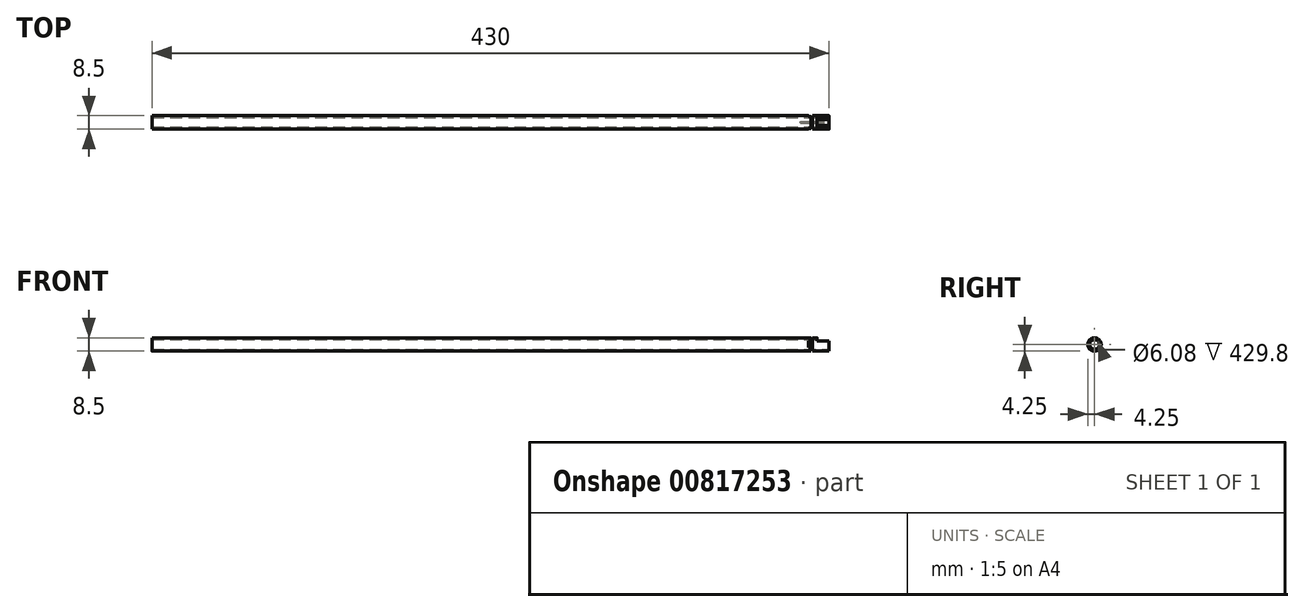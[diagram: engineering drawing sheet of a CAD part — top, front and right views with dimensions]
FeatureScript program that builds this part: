
annotation { "Feature Type Name" : "Feature", "Feature Type Description" : "" }
export const myFeature = defineFeature(function(context is Context, id is Id, definition is map)
    precondition{}
    {
        {
            var Q0;
            Q0=qCreatedBy(makeId("Front.planeOp"),FACE);
            var sketch = newSketch(context, id + "F0", { "sketchPlane" : qUnion([Q0])});
            skLineSegment(sketch, "E0", {"start": v(0, 0) * mm, "end": v(-418.5, 0) * mm});
            skLineSegment(sketch, "E1", {"start": v(-418.5, 0) * mm, "end": v(-418.5, 4.25) * mm});
            skLineSegment(sketch, "E2", {"start": v(-418.5, 4.25) * mm, "end": v(0, 4.25) * mm});
            skLineSegment(sketch, "E3", {"start": v(0, 4.25) * mm, "end": v(0, 0) * mm});
            skLineSegment(sketch, "E4", {"start": v(-418.5, 3.04) * mm, "end": v(0, 3.04) * mm});
            skLineSegment(sketch, "E5", {"start": v(0, 0) * mm, "end": v(1, 0) * mm});
            skLineSegment(sketch, "E6", {"start": v(1, 0) * mm, "end": v(1, 3.25) * mm});
            skLineSegment(sketch, "E7", {"start": v(1, 3.25) * mm, "end": v(0, 3.25) * mm});
            skLineSegment(sketch, "E8", {"start": v(0, 3.25) * mm, "end": v(0, 0) * mm});
            skLineSegment(sketch, "E9", {"start": v(0, 4.25) * mm, "end": v(6.8, 4.25) * mm, "construction": true});
            skLineSegment(sketch, "E10", {"start": v(1, 3.25) * mm, "end": v(1, 4.25) * mm});
            skLineSegment(sketch, "E11", {"start": v(1, 4.25) * mm, "end": v(11.5, 4.25) * mm});
            skLineSegment(sketch, "E12", {"start": v(11.5, 4.25) * mm, "end": v(11.5, 0) * mm});
            skLineSegment(sketch, "E13", {"start": v(11.5, 0) * mm, "end": v(1, 0) * mm});
            skSolve(sketch);
        }
        {
            var Q0;
            Q0 = qSketchRegion(id + "F0", true);
            var Q1;
            Q1=sQuery(id+"F0.wireOp",EDGE,"E0");
            revolve(context, id + "F1", {"surfaceOperationType" : NewSurfaceOperationType.NEW, "entities" : qUnion([Q0]), "axis" : qUnion([Q1]), "revolveType" : RevolveType.FULL});
        }
        {
            var Q0;
            Q0=qCreatedBy(makeId("Right.planeOp"),FACE);
            var sketch = newSketch(context, id + "F2", { "sketchPlane" : qUnion([Q0])});
            skCircle(sketch, "E14", {"center": v(0, 0) * mm, "radius": 3.04 * mm});
            skSolve(sketch);
        }
        {
            var Q0;
            Q0 = qSketchRegion(id + "F2", true);
            extrude(context, id + "F3", {"entities" : qUnion([Q0]), "operationType" : NewBodyOperationType.REMOVE, "endBound" : BoundingType.THROUGH_ALL, "oppositeDirection" : true, "depth" : 25 * mm, "offsetDistance" : 25 * mm});
        }
        {
            var Q0;
            Q0 = qSketchRegion(id + "F2", true);
            extrude(context, id + "F4", {"entities" : qUnion([Q0]), "operationType" : NewBodyOperationType.REMOVE, "depth" : 25 * mm, "offsetDistance" : 25 * mm});
        }
        {
            var Q0;
            Q0=qCreatedBy(makeId("Right.planeOp"),FACE);
            var sketch = newSketch(context, id + "F5", { "sketchPlane" : qUnion([Q0])});
            skLineSegment(sketch, "E15.bottom", {"start": v(5.62, 2.32) * mm, "end": v(-5.62, 2.32) * mm});
            skLineSegment(sketch, "E15.top", {"start": v(5.62, 4.32) * mm, "end": v(-5.62, 4.32) * mm});
            skLineSegment(sketch, "E15.left", {"start": v(5.62, 2.32) * mm, "end": v(5.62, 4.32) * mm});
            skLineSegment(sketch, "E15.right", {"start": v(-5.62, 2.32) * mm, "end": v(-5.62, 4.32) * mm});
            skPoint(sketch, "E15.middle", {"position": v(0, 3.32) * mm});
            skSolve(sketch);
        }
        {
            var Q0;
            Q0 = qSketchRegion(id + "F5", true);
            extrude(context, id + "F6", {"entities" : qUnion([Q0]), "operationType" : NewBodyOperationType.REMOVE, "depth" : 12.1 * mm, "hasOffset" : true, "offsetDistance" : 4 * mm, "offsetOppositeDirection" : true, "hasSecondDirection" : true, "secondDirectionOppositeDirection" : false, "secondDirectionDepth" : 4 * mm});
        }
        {
            var Q0;
            Q0=qCreatedBy(makeId("Front.planeOp"),FACE);
            var sketch = newSketch(context, id + "F7", { "sketchPlane" : qUnion([Q0])});
            skLineSegment(sketch, "E16.bottom", {"start": v(-1.5, -1.84) * mm, "end": v(0, -1.84) * mm});
            skLineSegment(sketch, "E16.top", {"start": v(-1.5, 2.16) * mm, "end": v(0, 2.16) * mm});
            skLineSegment(sketch, "E16.left", {"start": v(-1.5, -1.84) * mm, "end": v(-1.5, 2.16) * mm});
            skLineSegment(sketch, "E16.right", {"start": v(0, -1.84) * mm, "end": v(0, 2.16) * mm});
            skSolve(sketch);
        }
        {
            var Q0;
            Q0 = qSketchRegion(id + "F7", true);
            extrude(context, id + "F8", {"entities" : qUnion([Q0]), "operationType" : NewBodyOperationType.ADD, "depth" : 4.64 * mm, "offsetDistance" : 25 * mm, "hasSecondDirection" : true, "secondDirectionOppositeDirection" : false, "secondDirectionDepth" : 3.65 * mm});
        }
        {
            var Q0;
            Q0 = qSketchRegion(id + "F7", true);
            extrude(context, id + "F9", {"entities" : qUnion([Q0]), "operationType" : NewBodyOperationType.ADD, "oppositeDirection" : true, "depth" : 5.68 * mm, "offsetDistance" : 25 * mm, "hasSecondDirection" : true, "secondDirectionOppositeDirection" : true, "secondDirectionDepth" : 3.2 * mm});
        }
        {
            var Q0;
            Q0 = qSketchRegion(id + "F7", true);
            extrude(context, id + "F10", {"entities" : qUnion([Q0]), "operationType" : NewBodyOperationType.REMOVE, "depth" : 25 * mm, "offsetDistance" : 25 * mm, "hasSecondDirection" : true, "secondDirectionOppositeDirection" : false, "secondDirectionDepth" : 3.5 * mm});
        }
        {
            var Q0;
            Q0 = qSketchRegion(id + "F7", true);
            extrude(context, id + "F11", {"entities" : qUnion([Q0]), "operationType" : NewBodyOperationType.REMOVE, "oppositeDirection" : true, "depth" : 25 * mm, "offsetDistance" : 25 * mm, "hasSecondDirection" : true, "secondDirectionOppositeDirection" : true, "secondDirectionDepth" : 3.5 * mm});
        }
        {
            var Q0;
            Q0=qCreatedBy(makeId("Top.planeOp"),FACE);
            var sketch = newSketch(context, id + "F12", { "sketchPlane" : qUnion([Q0])});
            skLineSegment(sketch, "E17.bottom", {"start": v(-6.49, -0.5) * mm, "end": v(11.51, -0.5) * mm});
            skLineSegment(sketch, "E17.top", {"start": v(-6.49, 0.5) * mm, "end": v(11.51, 0.5) * mm});
            skLineSegment(sketch, "E17.left", {"start": v(-6.49, -0.5) * mm, "end": v(-6.49, 0.5) * mm});
            skLineSegment(sketch, "E17.right", {"start": v(11.51, -0.5) * mm, "end": v(11.51, 0.5) * mm});
            skSolve(sketch);
        }
        {
            var Q0;
            Q0 = qSketchRegion(id + "F12", true);
            extrude(context, id + "F13", {"entities" : qUnion([Q0]), "operationType" : NewBodyOperationType.REMOVE, "oppositeDirection" : true, "depth" : 7.5 * mm, "offsetDistance" : 25 * mm, "hasSecondDirection" : true, "secondDirectionOppositeDirection" : true, "secondDirectionDepth" : 3.72 * mm});
        }
        {
            var Q0;
            Q0=makeQuery(id+"F3.boolean.opBoolean","INTERSECT",EDGE,{"derivedFrom":[makeQuery(id+"F1.opRevolve","SWEPT_FACE",FACE,{"disambiguationData":[OSD([sQuery(id+"F0.wireOp",EDGE,"E1")])]}),makeQuery(id+"F3.opExtrude","SWEPT_FACE",FACE,{"disambiguationData":[OSD([sQuery(id+"F2.wireOp",EDGE,"E14")])]})]});
            chamfer(context, id + "F14", {"entities" : qUnion([Q0]), "width" : 0.2 * mm, "tangentPropagation" : true});
        }
        {
            var Q0;
            Q0=makeQuery(id+"F1.opRevolve","SWEPT_EDGE",EDGE,{"disambiguationData":[OSD([sQuery(id+"F0.wireOp",EDGE,"E1"),sQuery(id+"F0.wireOp",EDGE,"E2")])]});
            chamfer(context, id + "F15", {"entities" : qUnion([Q0]), "width" : 0.2 * mm, "tangentPropagation" : true});
        }
    });
